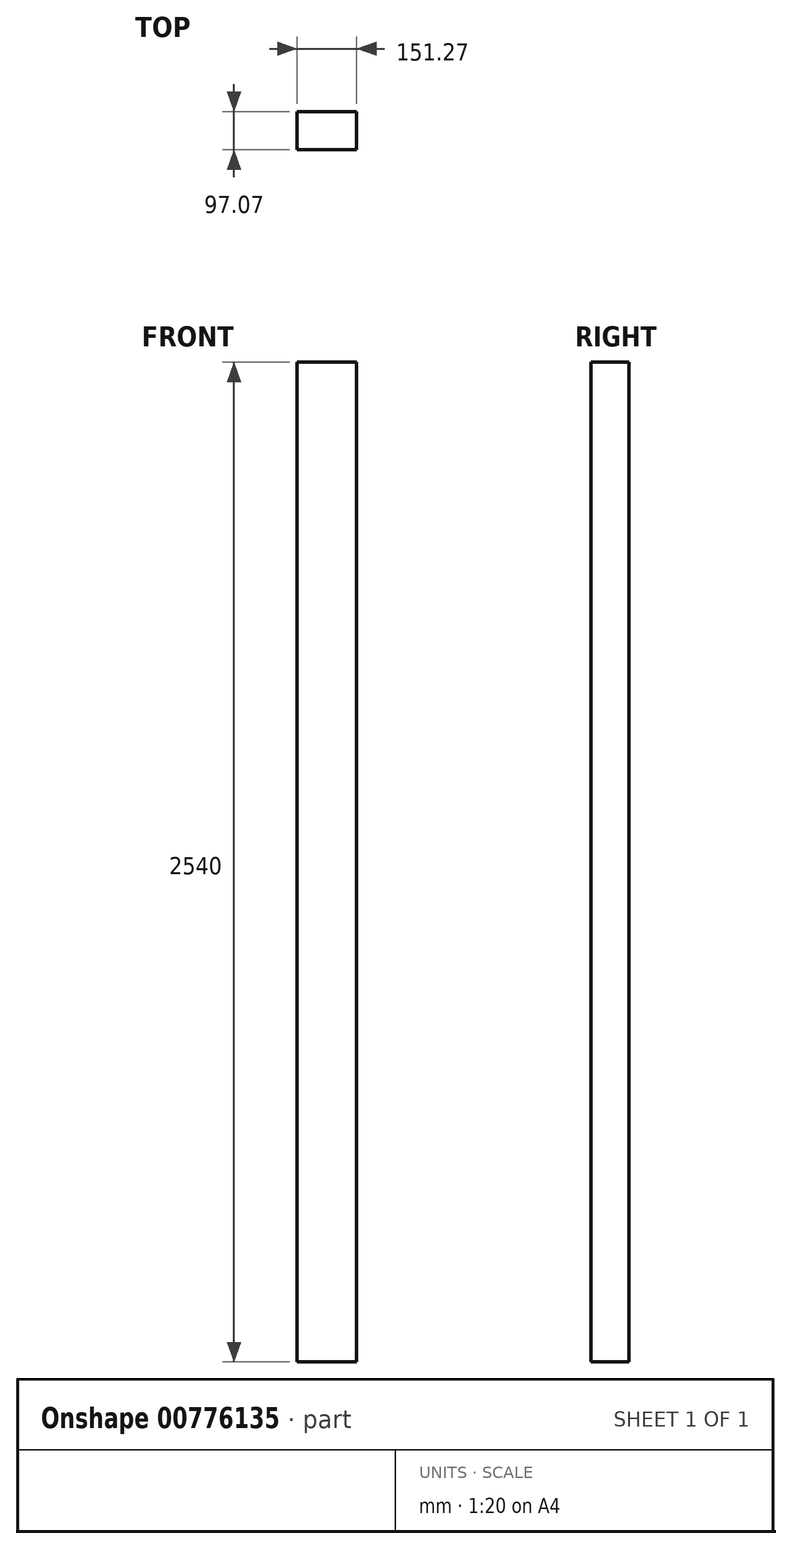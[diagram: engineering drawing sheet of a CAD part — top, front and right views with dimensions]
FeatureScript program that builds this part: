
annotation { "Feature Type Name" : "Feature", "Feature Type Description" : "" }
export const myFeature = defineFeature(function(context is Context, id is Id, definition is map)
    precondition{}
    {
        {
            var Q0;
            Q0=qCreatedBy(makeId("Top.planeOp"),FACE);
            var sketch = newSketch(context, id + "F0", { "sketchPlane" : qUnion([Q0])});
            skLineSegment(sketch, "E0.bottom", {"start": v(-53.1, 49.77) * mm, "end": v(98.18, 49.77) * mm});
            skLineSegment(sketch, "E0.top", {"start": v(-53.1, -47.3) * mm, "end": v(98.18, -47.3) * mm});
            skLineSegment(sketch, "E0.left", {"start": v(-53.1, 49.77) * mm, "end": v(-53.1, -47.3) * mm});
            skLineSegment(sketch, "E0.right", {"start": v(98.18, 49.77) * mm, "end": v(98.18, -47.3) * mm});
            skSolve(sketch);
        }
        {
            var Q0;
            Q0=makeQuery(id+"F0.imprint","IMPRINT",FACE,{"disambiguationData":[TD([[makeQuery(id+"F0.imprint","IMPRINT",EDGE,{"derivedFrom":sQuery(id+"F0.wireOp",EDGE,"E0.bottom")}),-1.0]])]});
            extrude(context, id + "F1", {"entities" : qUnion([Q0]), "depth" : 2540 * mm, "offsetDistance" : 25.4 * mm});
        }
    });
